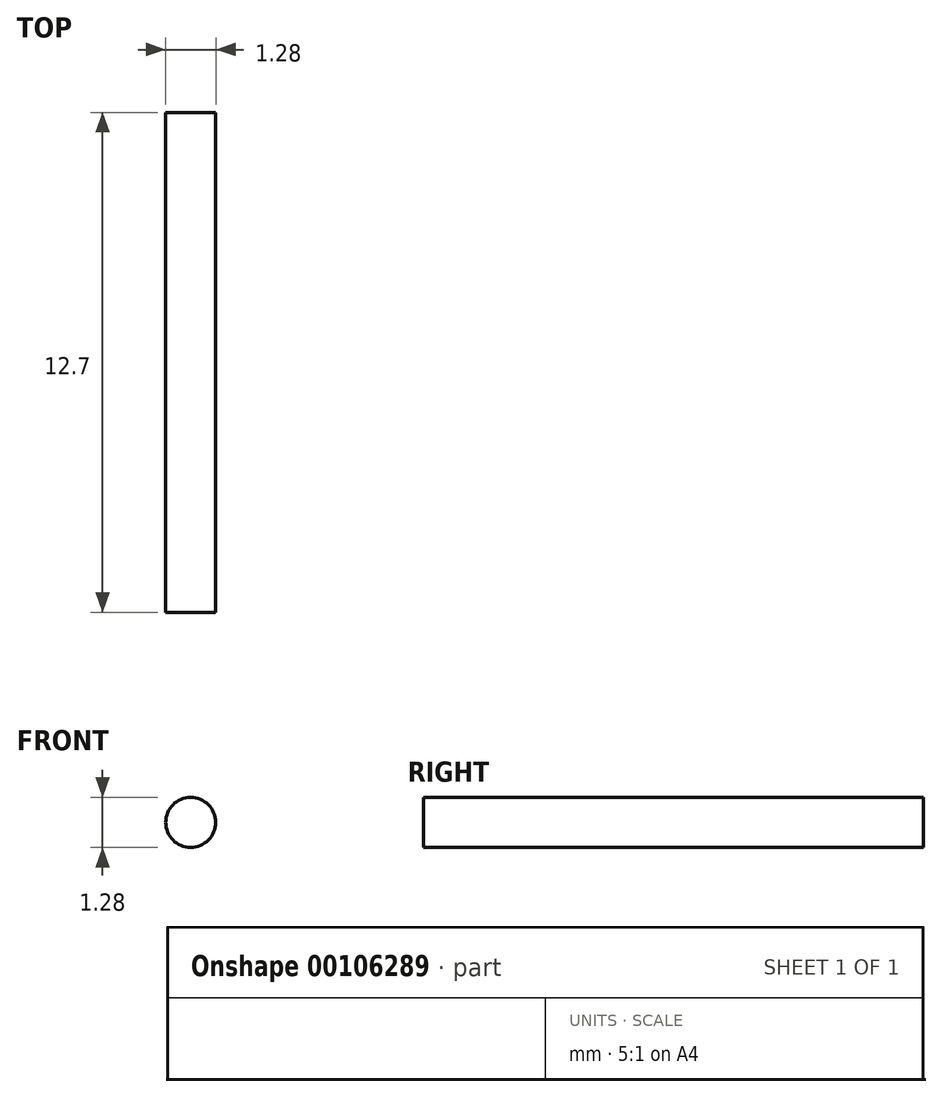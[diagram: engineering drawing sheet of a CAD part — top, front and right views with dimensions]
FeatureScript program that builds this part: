
annotation { "Feature Type Name" : "Feature", "Feature Type Description" : "" }
export const myFeature = defineFeature(function(context is Context, id is Id, definition is map)
    precondition{}
    {
        {
            var Q0;
            Q0=qCreatedBy(makeId("Front.planeOp"),FACE);
            var sketch = newSketch(context, id + "F0", { "sketchPlane" : qUnion([Q0])});
            skCircle(sketch, "E0", {"center": v(0, 0) * mm, "radius": 0.64 * mm});
            skSolve(sketch);
        }
        {
            var Q0;
            Q0 = qSketchRegion(id + "F0", true);
            extrude(context, id + "F1", {"entities" : qUnion([Q0]), "depth" : 12.7 * mm});
        }
    });
